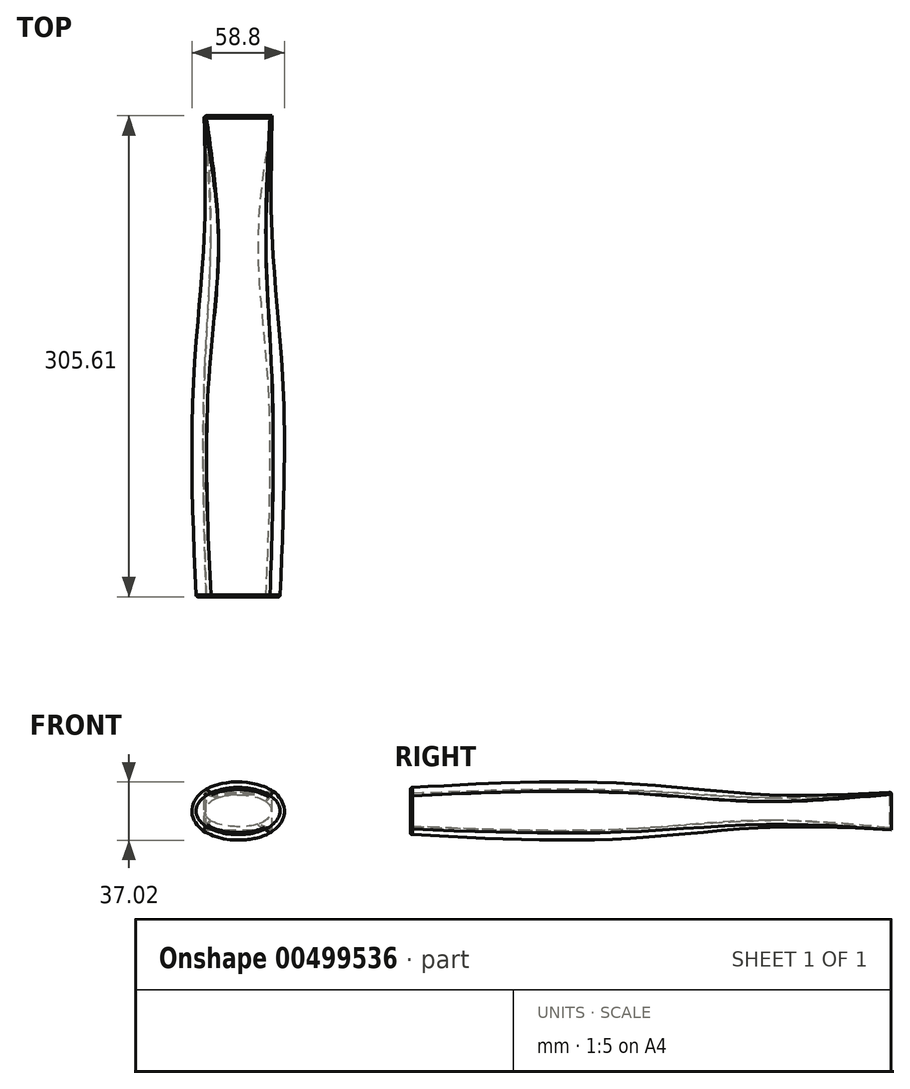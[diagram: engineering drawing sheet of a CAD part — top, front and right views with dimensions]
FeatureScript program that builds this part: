
annotation { "Feature Type Name" : "Feature", "Feature Type Description" : "" }
export const myFeature = defineFeature(function(context is Context, id is Id, definition is map)
    precondition{}
    {
        {
            var Q0;
            Q0=qCreatedBy(makeId("Front.planeOp"),FACE);
            cPlane(context, id + "F0", {"entities" : qUnion([Q0]), "cplaneType" : CPlaneType.OFFSET, "offset" : 33.02 * mm, "width" : 152.4 * mm, "height" : 152.4 * mm});
        }
        {
            var Q0;
            Q0=qCreatedBy(id+"F0.planeOp",FACE);
            cPlane(context, id + "F1", {"entities" : qUnion([Q0]), "cplaneType" : CPlaneType.OFFSET, "offset" : 43.69 * mm, "width" : 152.4 * mm, "height" : 152.4 * mm});
        }
        {
            var Q0;
            Q0=qCreatedBy(id+"F1.planeOp",FACE);
            var Q1;
            Q1 = qBodyType(qCreatedBy(id + "F6" ,EDGE), BodyType.WIRE);
            cPlane(context, id + "F2", {"entities" : qUnion([Q0, Q1]), "cplaneType" : CPlaneType.OFFSET, "offset" : 84.07 * mm, "width" : 152.4 * mm, "height" : 152.4 * mm});
        }
        {
            var Q0;
            Q0=qCreatedBy(id+"F2.planeOp",FACE);
            cPlane(context, id + "F3", {"entities" : qUnion([Q0]), "cplaneType" : CPlaneType.OFFSET, "offset" : 144.78 * mm, "width" : 152.4 * mm, "height" : 152.4 * mm});
        }
        {
            var Q0;
            Q0=qCreatedBy(makeId("Front.planeOp"),FACE);
            var sketch = newSketch(context, id + "F4", { "sketchPlane" : qUnion([Q0])});
            skLineSegment(sketch, "E0.bottom", {"start": v(-21.59, -11.97) * mm, "end": v(21.6, -11.97) * mm});
            skLineSegment(sketch, "E0.top", {"start": v(-21.6, 11.97) * mm, "end": v(21.59, 11.97) * mm});
            skLineSegment(sketch, "E0.left", {"start": v(-21.59, -11.97) * mm, "end": v(-21.6, 11.97) * mm});
            skLineSegment(sketch, "E0.right", {"start": v(21.6, -11.97) * mm, "end": v(21.59, 11.97) * mm});
            skPoint(sketch, "E0.middle", {"position": v(0, 0) * mm});
            skSolve(sketch);
        }
        {
            var Q0;
            Q0=qCreatedBy(id+"F1.planeOp",FACE);
            var sketch = newSketch(context, id + "F5", { "sketchPlane" : qUnion([Q0])});
            skEllipse(sketch, "E1", {"center": v(0, 0) * mm, "majorRadius": 21.6 * mm, "minorRadius": 10.29 * mm, "majorAxis": v(-1, 0)});
            skSolve(sketch);
        }
        {
            var Q0;
            Q0=qCreatedBy(id+"F2.planeOp",FACE);
            var sketch = newSketch(context, id + "F6", { "sketchPlane" : qUnion([Q0])});
            skEllipse(sketch, "E2", {"center": v(0, 0) * mm, "majorRadius": 27.94 * mm, "minorRadius": 17.04 * mm, "majorAxis": v(-1, 0)});
            skSolve(sketch);
        }
        {
            var Q0;
            Q0=qCreatedBy(id+"F3.planeOp",FACE);
            var sketch = newSketch(context, id + "F7", { "sketchPlane" : qUnion([Q0])});
            skEllipse(sketch, "E3", {"center": v(0, 0) * mm, "majorRadius": 26.67 * mm, "minorRadius": 14.93 * mm, "majorAxis": v(-1, 0)});
            skSolve(sketch);
        }
        {
            var Q0;
            Q0=makeQuery(id+"F4.imprint","IMPRINT",FACE,{"disambiguationData":[TD([[makeQuery(id+"F4.imprint","IMPRINT",EDGE,{"derivedFrom":sQuery(id+"F4.wireOp",EDGE,"E0.bottom")}),1.0]])]});
            var Q1;
            Q1=makeQuery(id+"F5.imprint","IMPRINT",FACE,{"disambiguationData":[TD([[makeQuery(id+"F5.imprint","IMPRINT",EDGE,{"derivedFrom":sQuery(id+"F5.wireOp",EDGE,"E1")}),1.0]])]});
            var Q2;
            Q2 = qSketchRegion(id + "F6", true);
            var Q3;
            Q3 = qSketchRegion(id + "F7", true);
            loft(context, id + "F8", {"sheetProfilesArray" : [{ "sheetProfileEntities" : qUnion([Q0]) }, { "sheetProfileEntities" : qUnion([Q1]) }, { "sheetProfileEntities" : qUnion([Q2]) }, { "sheetProfileEntities" : qUnion([Q3]) }]});
        }
        {
            var Q0;
            {var subQ0=sQuery(id+"F5.wireOp",EDGE,"E1");var subQ1=sQuery(id+"F4.wireOp",EDGE,"E0.left");var subQ2=sQuery(id+"F4.wireOp",EDGE,"E0.right");var subQ3=sQuery(id+"F4.wireOp",EDGE,"E0.top");var subQ4=sQuery(id+"F4.wireOp",EDGE,"E0.bottom");Q0=makeQuery(id+"F8.opLoft","SWEPT_FACE",FACE,{"disambiguationData":[OSD([subQ4,subQ3,subQ1,subQ2,subQ0]),TDD([makeQuery(id+"F4.imprint","INTERSECT",VERTEX,{"derivedFrom":[subQ4,subQ1]}),makeQuery(id+"F4.imprint","INTERSECT",VERTEX,{"derivedFrom":[subQ3,subQ1]}),makeQuery(id+"F4.imprint","INTERSECT",VERTEX,{"derivedFrom":[subQ3,subQ2]}),makeQuery(id+"F4.imprint","IMPRINT",EDGE,{"derivedFrom":subQ1}),makeQuery(id+"F5.imprint","IMPRINT",EDGE,{"derivedFrom":subQ0})])]});}
            var Q1;
            {var subQ0=sQuery(id+"F5.wireOp",EDGE,"E1");var subQ1=sQuery(id+"F4.wireOp",EDGE,"E0.right");var subQ2=sQuery(id+"F4.wireOp",EDGE,"E0.top");var subQ3=sQuery(id+"F4.wireOp",EDGE,"E0.bottom");var subQ4=sQuery(id+"F4.wireOp",EDGE,"E0.left");Q1=makeQuery(id+"F8.opLoft","SWEPT_FACE",FACE,{"disambiguationData":[OSD([subQ3,subQ2,subQ4,subQ1,subQ0]),TDD([makeQuery(id+"F4.imprint","INTERSECT",VERTEX,{"derivedFrom":[subQ3,subQ4]}),makeQuery(id+"F4.imprint","INTERSECT",VERTEX,{"derivedFrom":[subQ3,subQ1]}),makeQuery(id+"F4.imprint","INTERSECT",VERTEX,{"derivedFrom":[subQ2,subQ1]}),makeQuery(id+"F4.imprint","IMPRINT",EDGE,{"derivedFrom":subQ1}),makeQuery(id+"F5.imprint","IMPRINT",EDGE,{"derivedFrom":subQ0})])]});}
            fillet(context, id + "F9", {"entities" : qUnion([Q0, Q1]), "radius" : 1.27 * mm, "tangentPropagation" : true, "allowEdgeOverflow" : false});
        }
    });
